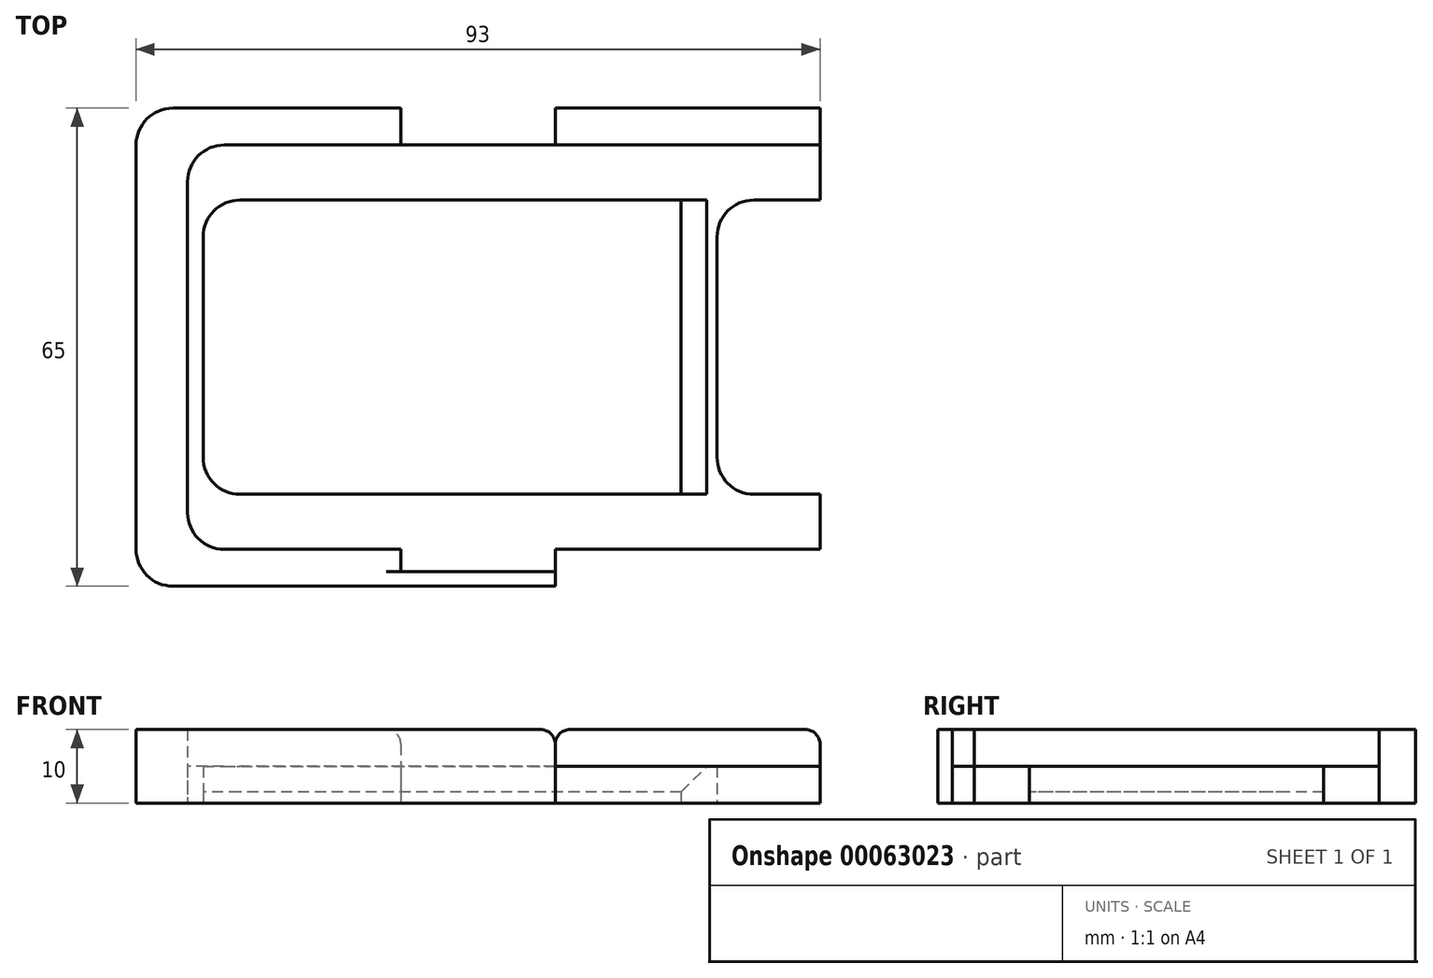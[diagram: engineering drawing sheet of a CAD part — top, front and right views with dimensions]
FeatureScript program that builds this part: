
annotation { "Feature Type Name" : "Feature", "Feature Type Description" : "" }
export const myFeature = defineFeature(function(context is Context, id is Id, definition is map)
    precondition{}
    {
        {
            var Q0;
            Q0=qCreatedBy(makeId("Top.planeOp"),FACE);
            var sketch = newSketch(context, id + "F0", { "sketchPlane" : qUnion([Q0])});
            skLineSegment(sketch, "E0.rect.bottom", {"start": v(46.5, -32.5) * mm, "end": v(-41.5, -32.5) * mm});
            skLineSegment(sketch, "E0.rect.top", {"start": v(46.5, 32.5) * mm, "end": v(-41.5, 32.5) * mm});
            skLineSegment(sketch, "E0.rect.left", {"start": v(46.5, -32.5) * mm, "end": v(46.5, 32.5) * mm});
            skLineSegment(sketch, "E0.rect.right", {"start": v(-46.5, -27.5) * mm, "end": v(-46.5, 27.5) * mm});
            skPoint(sketch, "E0.rect.middle", {"position": v(0, 0) * mm});
            skLineSegment(sketch, "E1.bottom", {"start": v(-34.5, 27.5) * mm, "end": v(46.5, 27.5) * mm});
            skLineSegment(sketch, "E1.top", {"start": v(-34.5, -27.5) * mm, "end": v(46.5, -27.5) * mm});
            skLineSegment(sketch, "E1.left", {"start": v(-39.5, 22.5) * mm, "end": v(-39.5, -22.5) * mm});
            skLineSegment(sketch, "E1.right", {"start": v(46.5, 27.5) * mm, "end": v(46.5, -27.5) * mm});
            skPoint(sketch, "E2.startSnap0", {"position": v(0, 32.5) * mm});
            skLineSegment(sketch, "E3.rect.bottom", {"start": v(37.5, -20) * mm, "end": v(46.5, -20) * mm});
            skLineSegment(sketch, "E3.rect.top", {"start": v(37.5, 20) * mm, "end": v(46.5, 20) * mm});
            skLineSegment(sketch, "E3.rect.left", {"start": v(32.5, -15) * mm, "end": v(32.5, 15) * mm});
            skPoint(sketch, "E3.rect.middle", {"position": v(46.5, 0) * mm});
            skPoint(sketch, "E3.rect.right.end.orphan", {"position": v(60.5, 20) * mm});
            skPoint(sketch, "E4.orphan", {"position": v(60.5, -20) * mm});
            skPoint(sketch, "E5.visualSharp", {"position": v(32.5, 20) * mm});
            skArc(sketch, "E5.filletArc", {"start": v(37.5, 20) * mm, "mid": v(33.96, 18.54) * mm, "end": v(32.5, 15) * mm});
            skPoint(sketch, "E6.visualSharp", {"position": v(32.5, -20) * mm});
            skArc(sketch, "E6.filletArc", {"start": v(32.5, -15) * mm, "mid": v(33.96, -18.54) * mm, "end": v(37.5, -20) * mm});
            skLineSegment(sketch, "E7.bottom", {"start": v(27.62, 20) * mm, "end": v(-32.38, 20) * mm});
            skLineSegment(sketch, "E7.top", {"start": v(27.62, -20) * mm, "end": v(-32.38, -20) * mm});
            skLineSegment(sketch, "E7.left", {"start": v(27.62, 20) * mm, "end": v(27.62, -20) * mm});
            skLineSegment(sketch, "E7.right", {"start": v(-37.38, 15) * mm, "end": v(-37.38, -15) * mm});
            skPoint(sketch, "E8.visualSharp", {"position": v(-39.5, 27.5) * mm});
            skArc(sketch, "E8.filletArc", {"start": v(-34.5, 27.5) * mm, "mid": v(-38.04, 26.04) * mm, "end": v(-39.5, 22.5) * mm});
            skPoint(sketch, "E9.visualSharp", {"position": v(-39.5, -27.5) * mm});
            skArc(sketch, "E9.filletArc", {"start": v(-39.5, -22.5) * mm, "mid": v(-38.04, -26.04) * mm, "end": v(-34.5, -27.5) * mm});
            skPoint(sketch, "E10.visualSharp", {"position": v(-46.5, 32.5) * mm});
            skArc(sketch, "E10.filletArc", {"start": v(-41.5, 32.5) * mm, "mid": v(-45.04, 31.04) * mm, "end": v(-46.5, 27.5) * mm});
            skPoint(sketch, "E11.visualSharp", {"position": v(-46.5, -32.5) * mm});
            skArc(sketch, "E11.filletArc", {"start": v(-46.5, -27.5) * mm, "mid": v(-45.04, -31.04) * mm, "end": v(-41.5, -32.5) * mm});
            skPoint(sketch, "E12.visualSharp", {"position": v(-37.38, 20) * mm});
            skArc(sketch, "E12.filletArc", {"start": v(-32.38, 20) * mm, "mid": v(-35.91, 18.54) * mm, "end": v(-37.38, 15) * mm});
            skPoint(sketch, "E13.visualSharp", {"position": v(-37.38, -20) * mm});
            skArc(sketch, "E13.filletArc", {"start": v(-37.38, -15) * mm, "mid": v(-35.91, -18.54) * mm, "end": v(-32.38, -20) * mm});
            skLineSegment(sketch, "E14.rect.bottom", {"start": v(10.5, 27.5) * mm, "end": v(-10.5, 27.5) * mm});
            skLineSegment(sketch, "E14.rect.left", {"start": v(10.5, 27.5) * mm, "end": v(10.5, 32.5) * mm});
            skLineSegment(sketch, "E14.rect.right", {"start": v(-10.5, 27.5) * mm, "end": v(-10.5, 32.5) * mm});
            skLineSegment(sketch, "E15.rect.bottom", {"start": v(10.5, -32.5) * mm, "end": v(-10.5, -32.5) * mm});
            skLineSegment(sketch, "E15.rect.top", {"start": v(10.5, -22.5) * mm, "end": v(-10.5, -22.5) * mm});
            skLineSegment(sketch, "E15.rect.left", {"start": v(10.5, -32.5) * mm, "end": v(10.5, -22.5) * mm});
            skLineSegment(sketch, "E15.rect.right", {"start": v(-10.5, -32.5) * mm, "end": v(-10.5, -22.5) * mm});
            skPoint(sketch, "E15.rect.middle", {"position": v(0, -27.5) * mm});
            skLineSegment(sketch, "E16.rect.bottom", {"start": v(10.5, 30.5) * mm, "end": v(-10.5, 30.5) * mm});
            skLineSegment(sketch, "E16.rect.left", {"start": v(10.5, 30.5) * mm, "end": v(10.5, 32.5) * mm});
            skLineSegment(sketch, "E16.rect.right", {"start": v(-10.5, 30.5) * mm, "end": v(-10.5, 32.5) * mm});
            skPoint(sketch, "E14.rect.top.start.orphan", {"position": v(10.5, 37.5) * mm});
            skPoint(sketch, "E17.orphan", {"position": v(-10.5, 37.5) * mm});
            skPoint(sketch, "E18.orphan", {"position": v(-10.5, 34.5) * mm});
            skPoint(sketch, "E19.orphan", {"position": v(10.5, 34.5) * mm});
            skLineSegment(sketch, "E20.rect.bottom", {"start": v(10.5, -30.5) * mm, "end": v(-10.5, -30.5) * mm});
            skLineSegment(sketch, "E20.rect.left", {"start": v(10.5, -30.5) * mm, "end": v(10.5, -32.5) * mm});
            skLineSegment(sketch, "E20.rect.right", {"start": v(-10.5, -30.5) * mm, "end": v(-10.5, -32.5) * mm});
            skPoint(sketch, "E20.rect.middle", {"position": v(0, -32.5) * mm});
            skPoint(sketch, "E20.rect.top.start.orphan", {"position": v(10.5, -34.5) * mm});
            skPoint(sketch, "E21.orphan", {"position": v(-10.5, -34.5) * mm});
            skSolve(sketch);
        }
        {
            var Q0;
            {var subQ1=sQuery(id+"F0.wireOp",EDGE,"E1.bottom");Q0=makeQuery(id+"F0.imprint","IMPRINT",FACE,{"disambiguationData":[TD([[makeQuery(id+"F0.imprint","IMPRINT",EDGE,{"derivedFrom":subQ1}),-1.0]])]});}
            var Q1;
            {var subQ5=sQuery(id+"F0.wireOp",EDGE,"E15.rect.top");Q1=makeQuery(id+"F0.imprint","IMPRINT",FACE,{"disambiguationData":[TD([[makeQuery(id+"F0.imprint","IMPRINT",EDGE,{"derivedFrom":subQ5}),1.0]])]});}
            var Q2;
            {var subQ5=sQuery(id+"F0.wireOp",EDGE,"E14.rect.bottom");Q2=makeQuery(id+"F0.imprint","IMPRINT",FACE,{"disambiguationData":[TD([[makeQuery(id+"F0.imprint","IMPRINT",EDGE,{"derivedFrom":subQ5}),-1.0]])]});}
            var Q3;
            {var subQ5=sQuery(id+"F0.wireOp",EDGE,"E20.rect.bottom");Q3=makeQuery(id+"F0.imprint","IMPRINT",FACE,{"disambiguationData":[TD([[makeQuery(id+"F0.imprint","IMPRINT",EDGE,{"derivedFrom":subQ5}),-1.0]])]});}
            extrude(context, id + "F1", {"entities" : qUnion([Q0, Q1, Q2, Q3]), "depth" : 5 * mm});
        }
        {
            var Q0;
            Q0=makeQuery(id+"F0.imprint","IMPRINT",FACE,{"disambiguationData":[TD([[makeQuery(id+"F0.imprint","IMPRINT",EDGE,{"derivedFrom":sQuery(id+"F0.wireOp",EDGE,"E7.bottom")}),1.0]])]});
            extrude(context, id + "F2", {"entities" : qUnion([Q0]), "depth" : 1.5 * mm});
        }
        {
            var Q0;
            {var subQ0=sQuery(id+"F0.wireOp",EDGE,"E0.rect.bottom");Q0=makeQuery(id+"F0.imprint","IMPRINT",FACE,{"disambiguationData":[TD([[makeQuery(id+"F0.imprint","IMPRINT",EDGE,{"derivedFrom":subQ0}),-1.0]])]});}
            var Q1;
            {var subQ0=sQuery(id+"F0.wireOp",EDGE,"E0.rect.left");var subQ1=sQuery(id+"F0.wireOp",EDGE,"E0.rect.top");var subQ2=makeQuery(id+"F0.imprint","INTERSECT",VERTEX,{"derivedFrom":[subQ1,subQ0]});Q1=makeQuery(id+"F0.imprint","IMPRINT",FACE,{"disambiguationData":[TD([[makeQuery(id+"F0.imprint","IMPRINT",EDGE,{"disambiguationData":[TD([[subQ2,-1.0]])],"derivedFrom":subQ1}),1.0]])]});}
            var Q2;
            Q2=makeQuery(id+"F0.imprint","IMPRINT",FACE,{"disambiguationData":[TD([[makeQuery(id+"F0.imprint","IMPRINT",EDGE,{"derivedFrom":sQuery(id+"F0.wireOp",EDGE,"E0.rect.right")}),-1.0]])]});
            extrude(context, id + "F3", {"entities" : qUnion([Q0, Q1, Q2]), "depth" : 10 * mm});
        }
        {
            var Q0;
            {var subQ0=sQuery(id+"F0.wireOp",EDGE,"E0.rect.left");Q0=makeQuery(id+"F3.opExtrude","CAP_EDGE",EDGE,{"disambiguationData":[OSD([subQ0]),TDD([makeQuery(id+"F0.imprint","IMPRINT",EDGE,{"disambiguationData":[TD([[makeQuery(id+"F0.imprint","INTERSECT",VERTEX,{"derivedFrom":[sQuery(id+"F0.wireOp",EDGE,"E0.rect.top"),subQ0]}),1.0]])],"derivedFrom":subQ0})])],"isStart":false});}
            var Q1;
            {var subQ0=sQuery(id+"F0.wireOp",EDGE,"E0.rect.left");Q1=makeQuery(id+"F3.opExtrude","CAP_EDGE",EDGE,{"disambiguationData":[OSD([subQ0]),TDD([makeQuery(id+"F0.imprint","IMPRINT",EDGE,{"disambiguationData":[TD([[makeQuery(id+"F0.imprint","INTERSECT",VERTEX,{"derivedFrom":[sQuery(id+"F0.wireOp",EDGE,"E0.rect.bottom"),subQ0]}),-1.0]])],"derivedFrom":subQ0})])],"isStart":false});}
            var Q2;
            Q2=makeQuery(id+"F3.opExtrude","CAP_EDGE",EDGE,{"disambiguationData":[OSD([sQuery(id+"F0.wireOp",EDGE,"E14.rect.left")])],"isStart":false});
            var Q3;
            Q3=makeQuery(id+"F3.opExtrude","CAP_EDGE",EDGE,{"disambiguationData":[OSD([sQuery(id+"F0.wireOp",EDGE,"E15.rect.left")])],"isStart":false});
            var Q4;
            Q4=makeQuery(id+"F3.opExtrude","CAP_EDGE",EDGE,{"disambiguationData":[OSD([sQuery(id+"F0.wireOp",EDGE,"E15.rect.right")])],"isStart":false});
            var Q5;
            Q5=makeQuery(id+"F3.opExtrude","CAP_EDGE",EDGE,{"disambiguationData":[OSD([sQuery(id+"F0.wireOp",EDGE,"E14.rect.right")])],"isStart":false});
            fillet(context, id + "F4", {"entities" : qUnion([Q0, Q1, Q2, Q3, Q4, Q5]), "radius" : 2 * mm, "tangentPropagation" : true, "allowEdgeOverflow" : false});
        }
        {
            var Q0;
            Q0=makeQuery(id+"F1.opExtrude","CAP_EDGE",EDGE,{"disambiguationData":[OSD([sQuery(id+"F0.wireOp",EDGE,"E7.left")])],"isStart":false});
            chamfer(context, id + "F5", {"entities" : qUnion([Q0]), "width" : 3.5 * mm, "tangentPropagation" : true});
        }
    });
